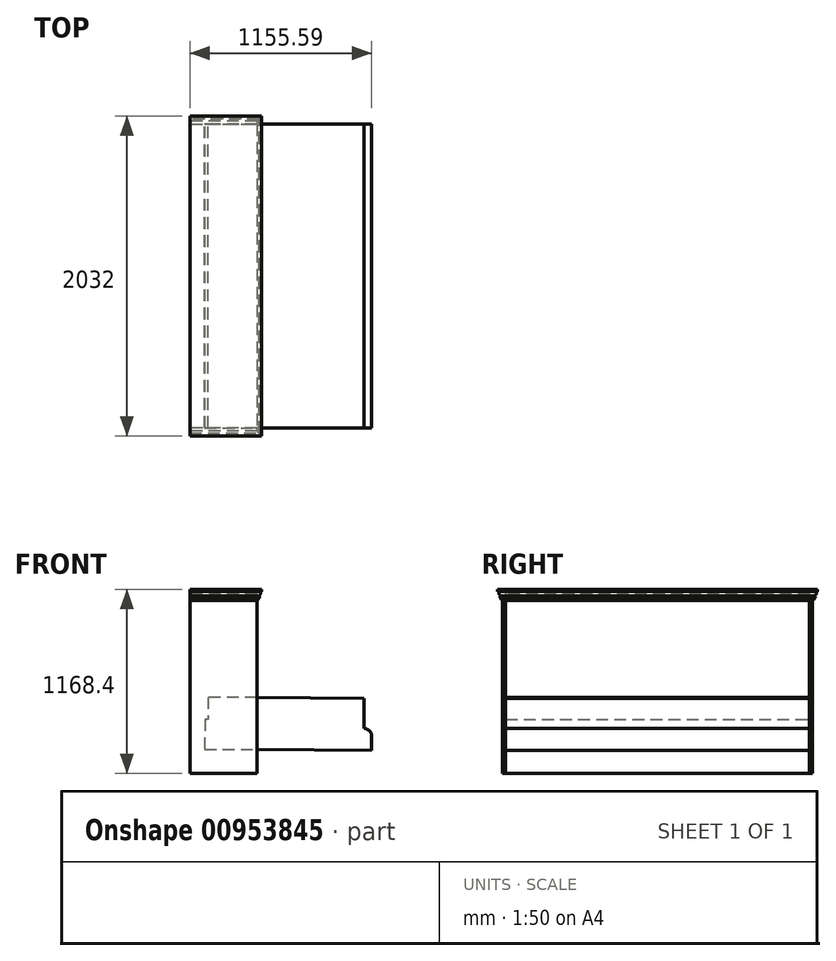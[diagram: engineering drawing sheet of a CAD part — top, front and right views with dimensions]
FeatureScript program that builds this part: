
annotation { "Feature Type Name" : "Feature", "Feature Type Description" : "" }
export const myFeature = defineFeature(function(context is Context, id is Id, definition is map)
    precondition{}
    {
        {
            var Q0;
            Q0=qCreatedBy(makeId("Front.planeOp"),FACE);
            var sketch = newSketch(context, id + "F0", { "sketchPlane" : qUnion([Q0])});
            skLineSegment(sketch, "E0.bottom", {"start": v(0, 0) * mm, "end": v(419.1, 0) * mm});
            skLineSegment(sketch, "E0.top", {"start": v(0, 1143) * mm, "end": v(419.1, 1143) * mm});
            skLineSegment(sketch, "E0.left", {"start": v(0, 0) * mm, "end": v(0, 1143) * mm});
            skLineSegment(sketch, "E0.right", {"start": v(419.1, 0) * mm, "end": v(419.1, 1143) * mm});
            skSolve(sketch);
        }
        {
            var Q0;
            Q0=makeQuery(id+"F0.imprint","IMPRINT",FACE,{"disambiguationData":[TD([[makeQuery(id+"F0.imprint","IMPRINT",EDGE,{"derivedFrom":sQuery(id+"F0.wireOp",EDGE,"E0.bottom")}),1.0]])]});
            var sketch = newSketch(context, id + "F1", { "sketchPlane" : qUnion([Q0])});
            skLineSegment(sketch, "E1", {"start": v(89.56, 344.57) * mm, "end": v(88.16, 154.08) * mm});
            skLineSegment(sketch, "E2", {"start": v(88.16, 154.08) * mm, "end": v(1148.58, 146.31) * mm});
            skLineSegment(sketch, "E3", {"start": v(1148.58, 146.31) * mm, "end": v(1149.23, 235.2) * mm});
            skLineSegment(sketch, "E4", {"start": v(1098.8, 286.38) * mm, "end": v(1098.8, 286.38) * mm});
            skLineSegment(sketch, "E5", {"start": v(1098.8, 286.38) * mm, "end": v(1100.2, 476.87) * mm});
            skLineSegment(sketch, "E6", {"start": v(1100.2, 476.87) * mm, "end": v(109.63, 484.13) * mm});
            skLineSegment(sketch, "E7", {"start": v(109.63, 484.13) * mm, "end": v(108.6, 344.43) * mm});
            skLineSegment(sketch, "E8", {"start": v(108.6, 344.43) * mm, "end": v(89.56, 344.57) * mm});
            skPoint(sketch, "E9", {"position": v(317.5, 254) * mm});
            skPoint(sketch, "E10.visualSharp", {"position": v(1149.6, 286) * mm});
            skArc(sketch, "E10.filletArc", {"start": v(1149.23, 235.2) * mm, "mid": v(1134.62, 271.24) * mm, "end": v(1098.8, 286.38) * mm});
            skLineSegment(sketch, "E11.bottom", {"start": v(0, 0) * mm, "end": v(419.1, 0) * mm, "construction": true});
            skLineSegment(sketch, "E11.top", {"start": v(0, 1143) * mm, "end": v(419.1, 1143) * mm, "construction": true});
            skLineSegment(sketch, "E11.left", {"start": v(0, 0) * mm, "end": v(0, 1143) * mm, "construction": true});
            skLineSegment(sketch, "E11.right", {"start": v(419.1, 0) * mm, "end": v(419.1, 1143) * mm, "construction": true});
            skSolve(sketch);
        }
        {
            var Q0;
            Q0 = qSketchRegion(id + "F1", true);
            extrude(context, id + "F2", {"entities" : qUnion([Q0]), "depth" : 1930.4 * mm, "offsetDistance" : 25.4 * mm});
        }
        {
            var Q0;
            Q0 = qSketchRegion(id + "F0", true);
            extrude(context, id + "F3", {"entities" : qUnion([Q0]), "operationType" : NewBodyOperationType.ADD, "oppositeDirection" : true, "depth" : 19.05 * mm, "offsetDistance" : 25.4 * mm});
        }
        {
            var Q0;
            Q0=makeQuery(id+"F2.opExtrude","CAP_FACE",FACE,{"disambiguationData":[OSD([sQuery(id+"F1.wireOp",EDGE,"E1"),sQuery(id+"F1.wireOp",EDGE,"E2"),sQuery(id+"F1.wireOp",EDGE,"E3"),sQuery(id+"F1.wireOp",EDGE,"E5"),sQuery(id+"F1.wireOp",EDGE,"E6"),sQuery(id+"F1.wireOp",EDGE,"E7"),sQuery(id+"F1.wireOp",EDGE,"E8"),sQuery(id+"F1.wireOp",EDGE,"E10.filletArc")])],"isStart":false});
            var sketch = newSketch(context, id + "F4", { "sketchPlane" : qUnion([Q0])});
            skPoint(sketch, "E12", {"position": v(419.1, 1143) * mm});
            skLineSegment(sketch, "E13.bottom", {"start": v(419.1, 1143) * mm, "end": v(0, 1143) * mm});
            skLineSegment(sketch, "E13.top", {"start": v(419.1, 0) * mm, "end": v(0, 0) * mm});
            skLineSegment(sketch, "E13.left", {"start": v(419.1, 1143) * mm, "end": v(419.1, 0) * mm});
            skLineSegment(sketch, "E13.right", {"start": v(0, 1143) * mm, "end": v(0, 0) * mm});
            skSolve(sketch);
        }
        {
            var Q0;
            Q0 = qSketchRegion(id + "F4", true);
            extrude(context, id + "F5", {"entities" : qUnion([Q0]), "operationType" : NewBodyOperationType.ADD, "depth" : 19.05 * mm, "offsetDistance" : 25.4 * mm});
        }
        {
            var Q0;
            Q0=makeQuery(id+"F3.opExtrude","SWEPT_FACE",FACE,{"disambiguationData":[OSD([sQuery(id+"F0.wireOp",EDGE,"E0.top")])]});
            var sketch = newSketch(context, id + "F6", { "sketchPlane" : qUnion([Q0])});
            skLineSegment(sketch, "E14.bottom", {"start": v(419.1, 19.05) * mm, "end": v(0, 19.05) * mm});
            skLineSegment(sketch, "E14.top", {"start": v(419.1, -1949.45) * mm, "end": v(0, -1949.45) * mm});
            skLineSegment(sketch, "E14.left", {"start": v(419.1, 19.05) * mm, "end": v(419.1, -1949.45) * mm});
            skLineSegment(sketch, "E14.right", {"start": v(0, 19.05) * mm, "end": v(0, -1949.45) * mm});
            skSolve(sketch);
        }
        {
            var Q0;
            Q0 = qSketchRegion(id + "F6", true);
            extrude(context, id + "F7", {"entities" : qUnion([Q0]), "operationType" : NewBodyOperationType.ADD, "depth" : 25.4 * mm, "offsetDistance" : 25.4 * mm});
        }
        {
            var Q0;
            Q0=makeQuery(id+"F7.boolean.opBoolean","MERGE",FACE,{"derivedFrom":[makeQuery(id+"F3.opExtrude","SWEPT_FACE",FACE,{"disambiguationData":[OSD([sQuery(id+"F0.wireOp",EDGE,"E0.left")])]}),makeQuery(id+"F5.opExtrude","SWEPT_FACE",FACE,{"disambiguationData":[OSD([sQuery(id+"F4.wireOp",EDGE,"E13.right")])]}),makeQuery(id+"F7.opExtrude","SWEPT_FACE",FACE,{"disambiguationData":[OSD([sQuery(id+"F6.wireOp",EDGE,"E14.right")])]})]});
            var sketch = newSketch(context, id + "F8", { "sketchPlane" : qUnion([Q0])});
            skLineSegment(sketch, "E15.bottom", {"start": v(-19.05, 1168.4) * mm, "end": v(1949.45, 1168.4) * mm});
            skLineSegment(sketch, "E15.top", {"start": v(-19.05, 0) * mm, "end": v(1949.45, 0) * mm});
            skLineSegment(sketch, "E15.left", {"start": v(-19.05, 1168.4) * mm, "end": v(-19.05, 0) * mm});
            skLineSegment(sketch, "E15.right", {"start": v(1949.45, 1168.4) * mm, "end": v(1949.45, 0) * mm});
            skSolve(sketch);
        }
        {
            var Q0;
            Q0 = qSketchRegion(id + "F8", true);
            extrude(context, id + "F9", {"entities" : qUnion([Q0]), "operationType" : NewBodyOperationType.ADD, "depth" : 6.35 * mm, "offsetDistance" : 25.4 * mm});
        }
        {
            var Q0;
            Q0=makeQuery(id+"F9.opExtrude","CAP_FACE",FACE,{"disambiguationData":[OSD([sQuery(id+"F8.wireOp",EDGE,"E15.bottom"),sQuery(id+"F8.wireOp",EDGE,"E15.top"),sQuery(id+"F8.wireOp",EDGE,"E15.left"),sQuery(id+"F8.wireOp",EDGE,"E15.right")])],"isStart":false});
            var sketch = newSketch(context, id + "F10", { "sketchPlane" : qUnion([Q0])});
            skLineSegment(sketch, "E16", {"start": v(1949.45, 1168.4) * mm, "end": v(1981.2, 1168.4) * mm});
            skLineSegment(sketch, "E17", {"start": v(1949.45, 1168.4) * mm, "end": v(1949.45, 1098.55) * mm});
            skLineSegment(sketch, "E18", {"start": v(1981.2, 1168.4) * mm, "end": v(1981.2, 1155.7) * mm});
            skFitSpline(sketch, "E19", {"points": [v(1981.2, 1155.7) * mm, v(1972.3, 1147.87) * mm, v(1971.4, 1137.5) * mm, v(1962.15, 1128.52) * mm], "startDerivative": vector(-56.77, -4.03) * mm, "endDerivative": vector(-38.32, -18.33) * mm});
            skLineSegment(sketch, "E20", {"start": v(1962.15, 1128.52) * mm, "end": v(1962.15, 1123.44) * mm});
            skArc(sketch, "E21", {"start": v(1962.15, 1116) * mm, "mid": v(1966.78, 1119.72) * mm, "end": v(1962.15, 1123.44) * mm});
            skLineSegment(sketch, "E22", {"start": v(1962.15, 1116) * mm, "end": v(1962.15, 1111.25) * mm});
            skFitSpline(sketch, "E23", {"points": [v(1962.15, 1111.25) * mm, v(1957.53, 1106.13) * mm, v(1954.62, 1102.8) * mm, v(1949.45, 1098.55) * mm], "startDerivative": vector(-0.07, -35.6) * mm, "endDerivative": vector(-38.4, -2.1) * mm});
            skSolve(sketch);
        }
        {
            var Q0;
            Q0=makeQuery(id+"F10.imprint","IMPRINT",FACE,{"disambiguationData":[TD([[makeQuery(id+"F10.imprint","IMPRINT",EDGE,{"derivedFrom":sQuery(id+"F10.wireOp",EDGE,"E16")}),-1.0]])]});
            var Q1;
            Q1=makeQuery(id+"F9.boolean.opBoolean","MERGE",EDGE,{"derivedFrom":[makeQuery(id+"F7.opExtrude","CAP_EDGE",EDGE,{"disambiguationData":[OSD([sQuery(id+"F6.wireOp",EDGE,"E14.top")])],"isStart":false}),makeQuery(id+"F9.opExtrude","SWEPT_EDGE",EDGE,{"disambiguationData":[OSD([sQuery(id+"F8.wireOp",EDGE,"E15.bottom"),sQuery(id+"F8.wireOp",EDGE,"E15.right")])]})]});
            var Q2;
            Q2=makeQuery(id+"F7.opExtrude","CAP_EDGE",EDGE,{"disambiguationData":[OSD([sQuery(id+"F6.wireOp",EDGE,"E14.left")])],"isStart":false});
            var Q3;
            Q3=makeQuery(id+"F9.boolean.opBoolean","MERGE",EDGE,{"derivedFrom":[makeQuery(id+"F7.opExtrude","CAP_EDGE",EDGE,{"disambiguationData":[OSD([sQuery(id+"F6.wireOp",EDGE,"E14.bottom")])],"isStart":false}),makeQuery(id+"F9.opExtrude","SWEPT_EDGE",EDGE,{"disambiguationData":[OSD([sQuery(id+"F8.wireOp",EDGE,"E15.bottom"),sQuery(id+"F8.wireOp",EDGE,"E15.left")])]})]});
            sweep(context, id + "F11", {"operationType" : NewBodyOperationType.ADD, "profiles" : qUnion([Q0]), "path" : qUnion([Q1, Q2, Q3])});
        }
    });
